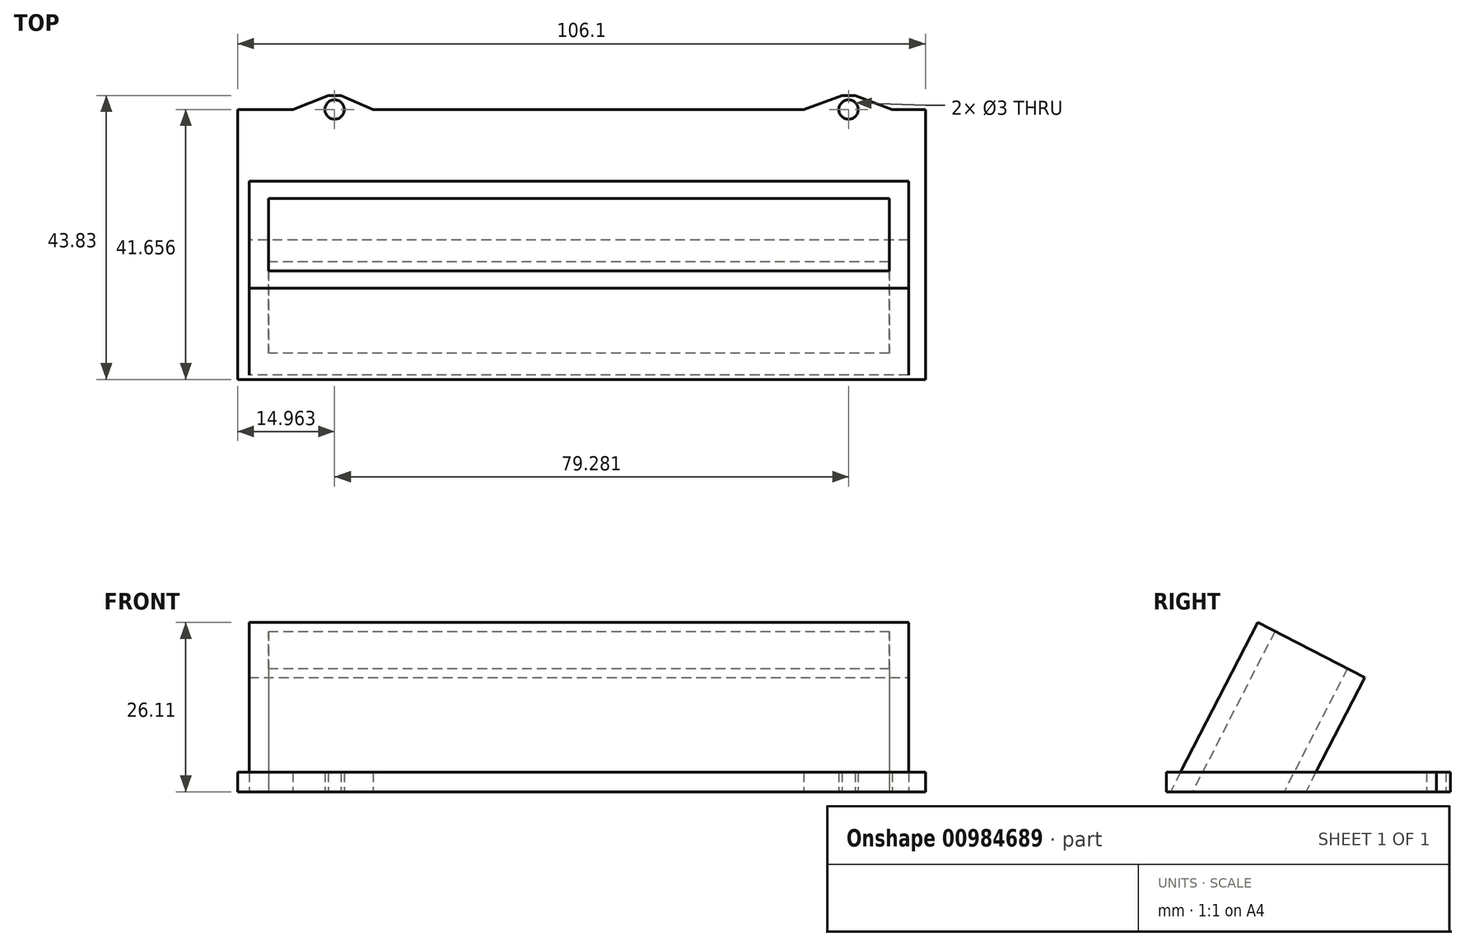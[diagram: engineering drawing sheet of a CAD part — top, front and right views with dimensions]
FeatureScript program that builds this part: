
annotation { "Feature Type Name" : "Feature", "Feature Type Description" : "" }
export const myFeature = defineFeature(function(context is Context, id is Id, definition is map)
    precondition{}
    {
        {
            var Q0;
            Q0=qCreatedBy(makeId("Top.planeOp"),FACE);
            var sketch = newSketch(context, id + "F0", { "sketchPlane" : qUnion([Q0])});
            skLineSegment(sketch, "E0.bottom", {"start": v(-44.5, 29.8) * mm, "end": v(51.24, 29.8) * mm});
            skLineSegment(sketch, "E0.top", {"start": v(-44.5, 17.23) * mm, "end": v(51.24, 17.23) * mm});
            skLineSegment(sketch, "E0.left", {"start": v(-44.5, 29.8) * mm, "end": v(-44.5, 17.23) * mm});
            skLineSegment(sketch, "E0.right", {"start": v(51.24, 29.8) * mm, "end": v(51.24, 17.23) * mm});
            skCircle(sketch, "E1.cCircle", {"center": v(-36.41, 23.5) * mm, "radius": 3.5 * mm, "construction": true});
            skPoint(sketch, "E1.cCircle.centerSnap0", {"position": v(-44.5, 23.5) * mm});
            skLineSegment(sketch, "E1.0", {"start": v(-38.43, 27) * mm, "end": v(-34.4, 27) * mm});
            skLineSegment(sketch, "E1.1", {"start": v(-34.4, 27) * mm, "end": v(-32.37, 23.5) * mm});
            skLineSegment(sketch, "E1.2", {"start": v(-32.37, 23.5) * mm, "end": v(-34.4, 20) * mm});
            skLineSegment(sketch, "E1.3", {"start": v(-34.4, 20) * mm, "end": v(-38.43, 20) * mm});
            skLineSegment(sketch, "E1.4", {"start": v(-38.43, 20) * mm, "end": v(-40.45, 23.5) * mm});
            skLineSegment(sketch, "E1.5", {"start": v(-40.45, 23.5) * mm, "end": v(-38.43, 27) * mm});
            skPoint(sketch, "E1.0.midPoint", {"position": v(-36.41, 27) * mm});
            skPoint(sketch, "E2.1.0.0", {"position": v(-25.81, 27) * mm});
            skLineSegment(sketch, "E2.1.0.1", {"start": v(-21.77, 23.5) * mm, "end": v(-23.8, 20) * mm});
            skCircle(sketch, "E2.1.0.2", {"center": v(-25.81, 23.5) * mm, "radius": 3.5 * mm, "construction": true});
            skLineSegment(sketch, "E2.1.0.3", {"start": v(-29.85, 23.5) * mm, "end": v(-27.83, 27) * mm});
            skLineSegment(sketch, "E2.1.0.4", {"start": v(-27.83, 20) * mm, "end": v(-29.85, 23.5) * mm});
            skLineSegment(sketch, "E2.1.0.5", {"start": v(-23.8, 20) * mm, "end": v(-27.83, 20) * mm});
            skLineSegment(sketch, "E2.1.0.6", {"start": v(-23.8, 27) * mm, "end": v(-21.77, 23.5) * mm});
            skLineSegment(sketch, "E2.1.0.7", {"start": v(-27.83, 27) * mm, "end": v(-23.8, 27) * mm});
            skPoint(sketch, "E2.2.0.0", {"position": v(-15.21, 27) * mm});
            skLineSegment(sketch, "E2.2.0.1", {"start": v(-11.17, 23.5) * mm, "end": v(-13.2, 20) * mm});
            skCircle(sketch, "E2.2.0.2", {"center": v(-15.21, 23.5) * mm, "radius": 3.5 * mm, "construction": true});
            skLineSegment(sketch, "E2.2.0.3", {"start": v(-19.25, 23.5) * mm, "end": v(-17.23, 27) * mm});
            skLineSegment(sketch, "E2.2.0.4", {"start": v(-17.23, 20) * mm, "end": v(-19.25, 23.5) * mm});
            skLineSegment(sketch, "E2.2.0.5", {"start": v(-13.2, 20) * mm, "end": v(-17.23, 20) * mm});
            skLineSegment(sketch, "E2.2.0.6", {"start": v(-13.2, 27) * mm, "end": v(-11.17, 23.5) * mm});
            skLineSegment(sketch, "E2.2.0.7", {"start": v(-17.23, 27) * mm, "end": v(-13.2, 27) * mm});
            skPoint(sketch, "E2.3.0.0", {"position": v(-4.61, 27) * mm});
            skLineSegment(sketch, "E2.3.0.1", {"start": v(-0.57, 23.5) * mm, "end": v(-2.6, 20) * mm});
            skCircle(sketch, "E2.3.0.2", {"center": v(-4.61, 23.5) * mm, "radius": 3.5 * mm, "construction": true});
            skLineSegment(sketch, "E2.3.0.3", {"start": v(-8.65, 23.5) * mm, "end": v(-6.63, 27) * mm});
            skLineSegment(sketch, "E2.3.0.4", {"start": v(-6.63, 20) * mm, "end": v(-8.65, 23.5) * mm});
            skLineSegment(sketch, "E2.3.0.5", {"start": v(-2.6, 20) * mm, "end": v(-6.63, 20) * mm});
            skLineSegment(sketch, "E2.3.0.6", {"start": v(-2.6, 27) * mm, "end": v(-0.57, 23.5) * mm});
            skLineSegment(sketch, "E2.3.0.7", {"start": v(-6.63, 27) * mm, "end": v(-2.6, 27) * mm});
            skLineSegment(sketch, "E2.direction1", {"start": v(-38.43, 20) * mm, "end": v(-27.83, 20) * mm, "construction": true});
            skLineSegment(sketch, "E3", {"start": v(-44.5, 23.5) * mm, "end": v(51.24, 23.5) * mm});
            skCircle(sketch, "E4", {"center": v(6.8, 23.5) * mm, "radius": 4 * mm});
            skCircle(sketch, "E5", {"center": v(16.77, 23.5) * mm, "radius": 3.25 * mm});
            skCircle(sketch, "E6", {"center": v(25.94, 23.5) * mm, "radius": 2.95 * mm});
            skCircle(sketch, "E7", {"center": v(33.6, 23.5) * mm, "radius": 2.5 * mm});
            skCircle(sketch, "E8", {"center": v(40.59, 23.5) * mm, "radius": 2 * mm});
            skCircle(sketch, "E9", {"center": v(46.32, 23.5) * mm, "radius": 1.75 * mm});
            skLineSegment(sketch, "E10.bottom", {"start": v(-47.5, 32.8) * mm, "end": v(54.24, 32.8) * mm});
            skLineSegment(sketch, "E10.top", {"start": v(-47.5, 14.23) * mm, "end": v(54.24, 14.23) * mm});
            skLineSegment(sketch, "E10.left", {"start": v(-47.5, 32.8) * mm, "end": v(-47.5, 14.23) * mm});
            skLineSegment(sketch, "E10.right", {"start": v(54.24, 32.8) * mm, "end": v(54.24, 14.23) * mm});
            skSolve(sketch);
        }
        {
            var Q0;
            Q0 = qSketchRegion(id + "F0", true);
            extrude(context, id + "F1", {"entities" : qUnion([Q0]), "depth" : 30 * mm, "offsetDistance" : 25 * mm});
        }
        {
            var Q0;
            Q0=qCreatedBy(makeId("Top.planeOp"),FACE);
            var sketch = newSketch(context, id + "F2", { "sketchPlane" : qUnion([Q0])});
            skLineSegment(sketch, "E11.bottom", {"start": v(-49.27, 12.27) * mm, "end": v(56.83, 12.27) * mm});
            skLineSegment(sketch, "E11.top", {"start": v(-49.27, 53.93) * mm, "end": v(56.83, 53.93) * mm});
            skLineSegment(sketch, "E11.left", {"start": v(-49.27, 12.27) * mm, "end": v(-49.27, 53.93) * mm});
            skLineSegment(sketch, "E11.right", {"start": v(56.83, 12.27) * mm, "end": v(56.83, 53.93) * mm});
            skCircle(sketch, "E12", {"center": v(-34.3, 53.93) * mm, "radius": 1.5 * mm});
            skCircle(sketch, "E13", {"center": v(44.97, 53.93) * mm, "radius": 1.5 * mm});
            skLineSegment(sketch, "E14", {"start": v(-35.3, 55.04) * mm, "end": v(-38.37, 53.93) * mm});
            skLineSegment(sketch, "E15", {"start": v(-33.3, 55.04) * mm, "end": v(-30.84, 53.93) * mm});
            skLineSegment(sketch, "E16", {"start": v(43.97, 55.04) * mm, "end": v(40.92, 53.93) * mm});
            skLineSegment(sketch, "E17", {"start": v(45.98, 55.04) * mm, "end": v(48.92, 53.93) * mm});
            skLineSegment(sketch, "E18", {"start": v(-40.77, 53.93) * mm, "end": v(-35.3, 56.1) * mm});
            skLineSegment(sketch, "E19", {"start": v(-33.3, 56.1) * mm, "end": v(-28.39, 53.93) * mm});
            skLineSegment(sketch, "E20", {"start": v(-35.3, 56.1) * mm, "end": v(-33.3, 56.1) * mm});
            skLineSegment(sketch, "E21", {"start": v(38.04, 53.93) * mm, "end": v(43.97, 56.1) * mm});
            skLineSegment(sketch, "E22", {"start": v(45.98, 56.1) * mm, "end": v(51.68, 53.93) * mm});
            skLineSegment(sketch, "E23", {"start": v(43.97, 56.1) * mm, "end": v(45.98, 56.1) * mm});
            skSolve(sketch);
        }
        {
            var Q0;
            Q0=makeQuery(id+"F2.imprint","IMPRINT",FACE,{"disambiguationData":[TD([[makeQuery(id+"F2.imprint","IMPRINT",EDGE,{"derivedFrom":sQuery(id+"F2.wireOp",EDGE,"E11.bottom")}),1.0]])]});
            var Q1;
            {var subQ0=sQuery(id+"F2.wireOp",EDGE,"E14");Q1=makeQuery(id+"F2.imprint","IMPRINT",FACE,{"disambiguationData":[TD([[makeQuery(id+"F2.imprint","IMPRINT",EDGE,{"derivedFrom":subQ0}),-1.0]])]});}
            var Q2;
            {var subQ0=sQuery(id+"F2.wireOp",EDGE,"E15");Q2=makeQuery(id+"F2.imprint","IMPRINT",FACE,{"disambiguationData":[TD([[makeQuery(id+"F2.imprint","IMPRINT",EDGE,{"derivedFrom":subQ0}),-1.0]])]});}
            var Q3;
            {var subQ0=sQuery(id+"F2.wireOp",EDGE,"E14");Q3=makeQuery(id+"F2.imprint","IMPRINT",FACE,{"disambiguationData":[TD([[makeQuery(id+"F2.imprint","IMPRINT",EDGE,{"derivedFrom":subQ0}),1.0]])]});}
            var Q4;
            {var subQ0=sQuery(id+"F2.wireOp",EDGE,"E16");Q4=makeQuery(id+"F2.imprint","IMPRINT",FACE,{"disambiguationData":[TD([[makeQuery(id+"F2.imprint","IMPRINT",EDGE,{"derivedFrom":subQ0}),-1.0]])]});}
            var Q5;
            {var subQ0=sQuery(id+"F2.wireOp",EDGE,"E16");Q5=makeQuery(id+"F2.imprint","IMPRINT",FACE,{"disambiguationData":[TD([[makeQuery(id+"F2.imprint","IMPRINT",EDGE,{"derivedFrom":subQ0}),1.0]])]});}
            var Q6;
            {var subQ0=sQuery(id+"F2.wireOp",EDGE,"E17");Q6=makeQuery(id+"F2.imprint","IMPRINT",FACE,{"disambiguationData":[TD([[makeQuery(id+"F2.imprint","IMPRINT",EDGE,{"derivedFrom":subQ0}),-1.0]])]});}
            extrude(context, id + "F3", {"entities" : qUnion([Q0, Q1, Q2, Q3, Q4, Q5, Q6]), "depth" : 3 * mm, "offsetDistance" : 25 * mm});
        }
        {
            var Q0;
            Q0=makeQuery(id+"F1.opExtrude","SWEPT_BODY",BODY,{"disambiguationData":[OSD([sQuery(id+"F0.wireOp",EDGE,"E0.bottom"),sQuery(id+"F0.wireOp",EDGE,"E0.top"),sQuery(id+"F0.wireOp",EDGE,"E0.left"),sQuery(id+"F0.wireOp",EDGE,"E0.right"),sQuery(id+"F0.wireOp",EDGE,"E10.bottom"),sQuery(id+"F0.wireOp",EDGE,"E10.top"),sQuery(id+"F0.wireOp",EDGE,"E10.left"),sQuery(id+"F0.wireOp",EDGE,"E10.right")])]});
            var Q1;
            Q1=makeQuery(id+"F3.opExtrude","CAP_EDGE",EDGE,{"disambiguationData":[OSD([sQuery(id+"F2.wireOp",EDGE,"E11.bottom")])],"isStart":false});
            transform(context, id + "F4", {"entities" : qUnion([Q0]), "transformType" : TransformType.ROTATION, "transformAxis" : qUnion([Q1]), "angle" : 27.22 * degree, "oppositeDirection" : true, "makeCopy" : false});
        }
        {
            var Q0;
            Q0=makeQuery(id+"F3.opExtrude","SWEPT_FACE",FACE,{"disambiguationData":[OSD([sQuery(id+"F2.wireOp",EDGE,"E11.right")])]});
            var sketch = newSketch(context, id + "F5", { "sketchPlane" : qUnion([Q0])});
            skLineSegment(sketch, "E24.bottom", {"start": v(12.27, 0) * mm, "end": v(53.6, 0) * mm});
            skLineSegment(sketch, "E24.top", {"start": v(12.27, -17.58) * mm, "end": v(53.6, -17.58) * mm});
            skLineSegment(sketch, "E24.left", {"start": v(12.27, 0) * mm, "end": v(12.27, -17.58) * mm});
            skLineSegment(sketch, "E24.right", {"start": v(53.6, 0) * mm, "end": v(53.6, -17.58) * mm});
            skSolve(sketch);
        }
        {
            var Q0;
            Q0=makeQuery(id+"F5.imprint","IMPRINT",FACE,{"disambiguationData":[TD([[makeQuery(id+"F5.imprint","IMPRINT",EDGE,{"derivedFrom":sQuery(id+"F5.wireOp",EDGE,"E24.bottom")}),-1.0]])]});
            extrude(context, id + "F6", {"entities" : qUnion([Q0]), "operationType" : NewBodyOperationType.REMOVE, "oppositeDirection" : true, "depth" : 119.8 * mm, "offsetDistance" : 25 * mm});
        }
    });
